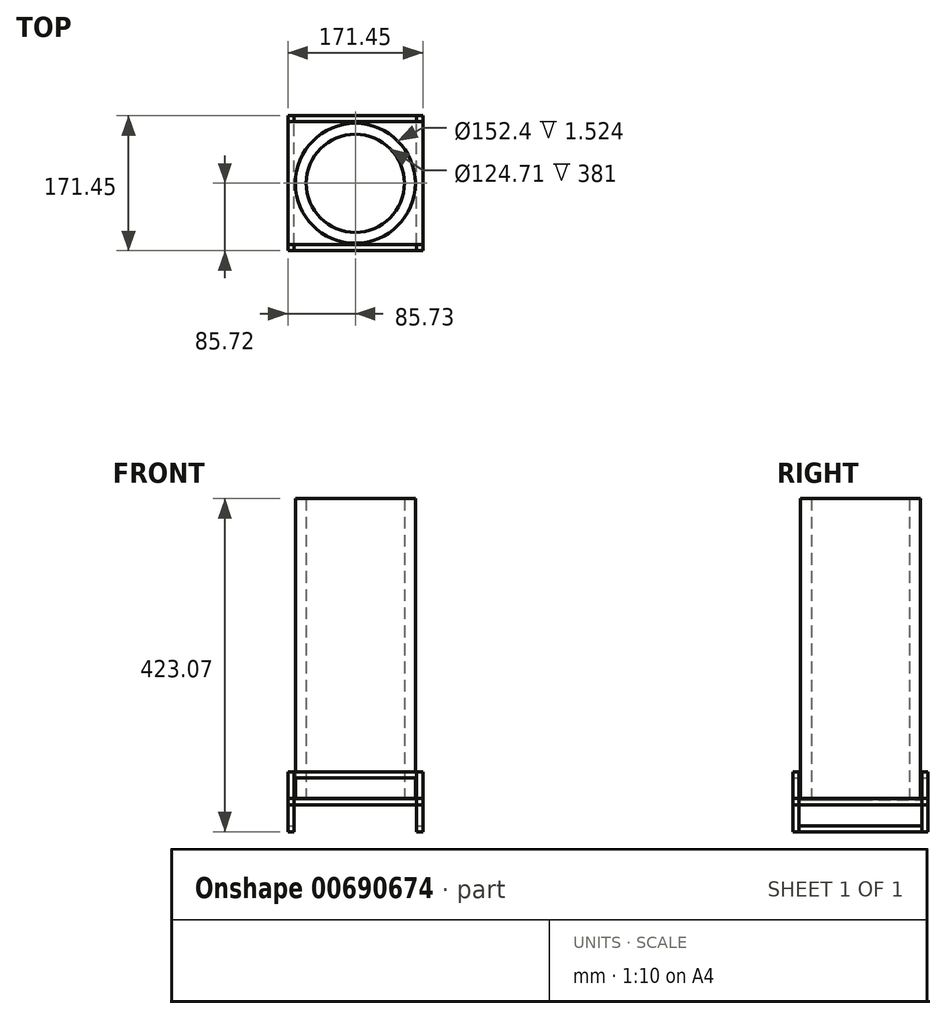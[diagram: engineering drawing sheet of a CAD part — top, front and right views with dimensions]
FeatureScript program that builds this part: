
annotation { "Feature Type Name" : "Feature", "Feature Type Description" : "" }
export const myFeature = defineFeature(function(context is Context, id is Id, definition is map)
    precondition{}
    {
        {
            var Q0;
            Q0=qCreatedBy(makeId("Top.planeOp"),FACE);
            var sketch = newSketch(context, id + "F0", { "sketchPlane" : qUnion([Q0])});
            skCircle(sketch, "E0", {"center": v(0, 0) * mm, "radius": 76.2 * mm});
            skCircle(sketch, "E1.0", {"center": v(0, 0) * mm, "radius": 62.36 * mm});
            skSolve(sketch);
        }
        {
            var Q0;
            Q0=qSketchRegion(id+"F0",true);
            extrude(context, id + "F1", {"entities" : qUnion([Q0]), "depth" : 381 * mm, "offsetDistance" : 25.4 * mm});
        }
        {
            var Q0;
            Q0=qCreatedBy(makeId("Top.planeOp"),FACE);
            cPlane(context, id + "F2", {"entities" : qUnion([Q0]), "cplaneType" : CPlaneType.OFFSET, "offset" : 3.97 * mm, "oppositeDirection" : true, "width" : 152.4 * mm, "height" : 152.4 * mm});
        }
        {
            var Q0;
            Q0=qCreatedBy(id+"F2.planeOp",FACE);
            var sketch = newSketch(context, id + "F3", { "sketchPlane" : qUnion([Q0])});
            skPoint(sketch, "E2.middle", {"position": v(0, 0) * mm});
            skLineSegment(sketch, "E3.left", {"start": v(-114.4, 10.1) * mm, "end": v(-114.4, -10.1) * mm});
            skLineSegment(sketch, "E4", {"start": v(-85.73, 85.73) * mm, "end": v(85.73, -85.73) * mm, "construction": true});
            skLineSegment(sketch, "E5", {"start": v(85.73, 85.73) * mm, "end": v(73.61, 73.61) * mm, "construction": true});
            skLineSegment(sketch, "E6.bottom", {"start": v(85.73, 85.73) * mm, "end": v(78.06, 85.73) * mm});
            skLineSegment(sketch, "E6.top", {"start": v(85.73, 78.06) * mm, "end": v(78.06, 78.06) * mm});
            skLineSegment(sketch, "E6.left", {"start": v(85.73, 85.73) * mm, "end": v(85.73, 78.06) * mm});
            skLineSegment(sketch, "E6.right", {"start": v(78.06, 85.73) * mm, "end": v(78.06, 78.06) * mm});
            skLineSegment(sketch, "E7.bottom", {"start": v(-85.72, 85.73) * mm, "end": v(85.72, 85.73) * mm});
            skLineSegment(sketch, "E7.top", {"start": v(-85.72, -85.72) * mm, "end": v(85.72, -85.72) * mm});
            skLineSegment(sketch, "E7.left", {"start": v(-85.73, 85.72) * mm, "end": v(-85.73, -85.72) * mm});
            skLineSegment(sketch, "E7.right", {"start": v(85.72, 85.72) * mm, "end": v(85.72, -85.72) * mm});
            skSolve(sketch);
        }
        {
            var Q0;
            Q0 = qSketchRegion(id + "F3", true);
            extrude(context, id + "F4", {"entities" : qUnion([Q0]), "endBound" : BoundingType.SYMMETRIC, "oppositeDirection" : true, "depth" : 7.94 * mm, "offsetDistance" : 25.4 * mm});
        }
        {
            var Q0;
            Q0 = qSketchRegion(id + "F0", true);
            extrude(context, id + "F5", {"entities" : qUnion([Q0]), "operationType" : NewBodyOperationType.REMOVE, "oppositeDirection" : true, "depth" : 1.52 * mm, "offsetDistance" : 25.4 * mm});
        }
        {
            var Q0;
            {var subQ0=sQuery(id+"F3.wireOp",EDGE,"E6.top");Q0=makeQuery(id+"F3.imprint","IMPRINT",FACE,{"disambiguationData":[TD([[makeQuery(id+"F3.imprint","IMPRINT",EDGE,{"derivedFrom":subQ0}),-1.0]])]});}
            extrude(context, id + "F6", {"entities" : qUnion([Q0]), "depth" : 38.1 * mm, "offsetDistance" : 25.4 * mm, "hasSecondDirection" : true, "secondDirectionOppositeDirection" : true, "secondDirectionDepth" : 38.1 * mm});
        }
        {
            var Q0;
            Q0=makeQuery(id+"F6.opExtrude","SWEPT_BODY",BODY,{"disambiguationData":[OSD([sQuery(id+"F3.wireOp",EDGE,"E6.top"),sQuery(id+"F3.wireOp",EDGE,"E6.right"),sQuery(id+"F3.wireOp",EDGE,"E7.bottom"),sQuery(id+"F3.wireOp",EDGE,"E7.right")])]});
            var Q1;
            Q1=sQuery(id+"F0.wireOp",EDGE,"E1.0");
            circularPattern(context, id + "F7", {"entities" : qUnion([Q0]), "axis" : qUnion([Q1]), "angle" : 360 * degree, "instanceCount" : 4, "equalSpace" : true});
        }
        {
            var Q0;
            Q0=makeQuery(id+"F7.opPattern","COPY",FACE,{"derivedFrom":makeQuery(id+"F6.opExtrude","SWEPT_FACE",FACE,{"disambiguationData":[OSD([sQuery(id+"F3.wireOp",EDGE,"E6.top")])]}),"instanceName":"1"});
            var sketch = newSketch(context, id + "F8", { "sketchPlane" : qUnion([Q0])});
            skLineSegment(sketch, "E8.bottom", {"start": v(78.06, 34.13) * mm, "end": v(85.73, 34.13) * mm});
            skLineSegment(sketch, "E8.top", {"start": v(78.06, 26.47) * mm, "end": v(85.73, 26.47) * mm});
            skLineSegment(sketch, "E8.left", {"start": v(78.06, 34.13) * mm, "end": v(78.06, 26.47) * mm});
            skLineSegment(sketch, "E8.right", {"start": v(85.73, 34.13) * mm, "end": v(85.73, 26.47) * mm});
            skLineSegment(sketch, "E9.0.0", {"start": v(-85.73, -42.07) * mm, "end": v(-78.06, -42.07) * mm, "construction": true});
            skLineSegment(sketch, "E9.0.1", {"start": v(-78.06, -42.07) * mm, "end": v(-78.06, 34.13) * mm, "construction": true});
            skLineSegment(sketch, "E9.0.2", {"start": v(-78.06, 34.13) * mm, "end": v(-85.73, 34.13) * mm, "construction": true});
            skLineSegment(sketch, "E9.0.3", {"start": v(-85.73, 34.13) * mm, "end": v(-85.73, -42.07) * mm, "construction": true});
            skLineSegment(sketch, "E10", {"start": v(78.06, 26.47) * mm, "end": v(-78.06, 26.47) * mm, "construction": true});
            skLineSegment(sketch, "E11", {"start": v(0, 26.47) * mm, "end": v(0, 61.38) * mm, "construction": true});
            skLineSegment(sketch, "E12.MirrorCS", {"start": v(-78.06, 34.13) * mm, "end": v(-85.73, 34.13) * mm});
            skLineSegment(sketch, "E13.MirrorCS", {"start": v(-78.06, 26.47) * mm, "end": v(-85.73, 26.47) * mm});
            skLineSegment(sketch, "E14.MirrorCS", {"start": v(-78.06, 34.13) * mm, "end": v(-78.06, 26.47) * mm});
            skLineSegment(sketch, "E15.MirrorCS", {"start": v(-85.73, 34.13) * mm, "end": v(-85.73, 26.47) * mm});
            skSolve(sketch);
        }
        {
            var Q0;
            Q0 = qSketchRegion(id + "F8", true);
            extrude(context, id + "F9", {"entities" : qUnion([Q0]), "endBound" : BoundingType.UP_TO_NEXT, "depth" : 25.4 * mm, "offsetDistance" : 25.4 * mm});
        }
        {
            var Q0;
            Q0=makeQuery(id+"F6.opExtrude","SWEPT_FACE",FACE,{"disambiguationData":[OSD([sQuery(id+"F3.wireOp",EDGE,"E6.top")])]});
            var sketch = newSketch(context, id + "F10", { "sketchPlane" : qUnion([Q0])});
            skLineSegment(sketch, "E16.bottom", {"start": v(78.06, -42.07) * mm, "end": v(85.73, -42.07) * mm});
            skLineSegment(sketch, "E16.top", {"start": v(78.06, -34.4) * mm, "end": v(85.73, -34.4) * mm});
            skLineSegment(sketch, "E16.left", {"start": v(78.06, -42.07) * mm, "end": v(78.06, -34.4) * mm});
            skLineSegment(sketch, "E16.right", {"start": v(85.73, -42.07) * mm, "end": v(85.73, -34.4) * mm});
            skLineSegment(sketch, "E17", {"start": v(78.06, -34.4) * mm, "end": v(-78.06, -34.4) * mm, "construction": true});
            skLineSegment(sketch, "E18.0", {"start": v(-78.06, 34.13) * mm, "end": v(-78.06, -42.07) * mm, "construction": true});
            skLineSegment(sketch, "E19", {"start": v(0, -34.4) * mm, "end": v(0, -29.74) * mm, "construction": true});
            skLineSegment(sketch, "E20.MirrorCS", {"start": v(-85.73, -42.07) * mm, "end": v(-85.73, -34.4) * mm});
            skLineSegment(sketch, "E21.MirrorCS", {"start": v(-78.06, -42.07) * mm, "end": v(-85.73, -42.07) * mm});
            skLineSegment(sketch, "E22.MirrorCS", {"start": v(-78.06, -34.4) * mm, "end": v(-85.73, -34.4) * mm});
            skLineSegment(sketch, "E23.MirrorCS", {"start": v(-78.06, -42.07) * mm, "end": v(-78.06, -34.4) * mm});
            skSolve(sketch);
        }
        {
            var Q0;
            Q0 = qSketchRegion(id + "F10", true);
            extrude(context, id + "F11", {"entities" : qUnion([Q0]), "endBound" : BoundingType.UP_TO_NEXT, "depth" : 25.4 * mm, "offsetDistance" : 25.4 * mm});
        }
    });
